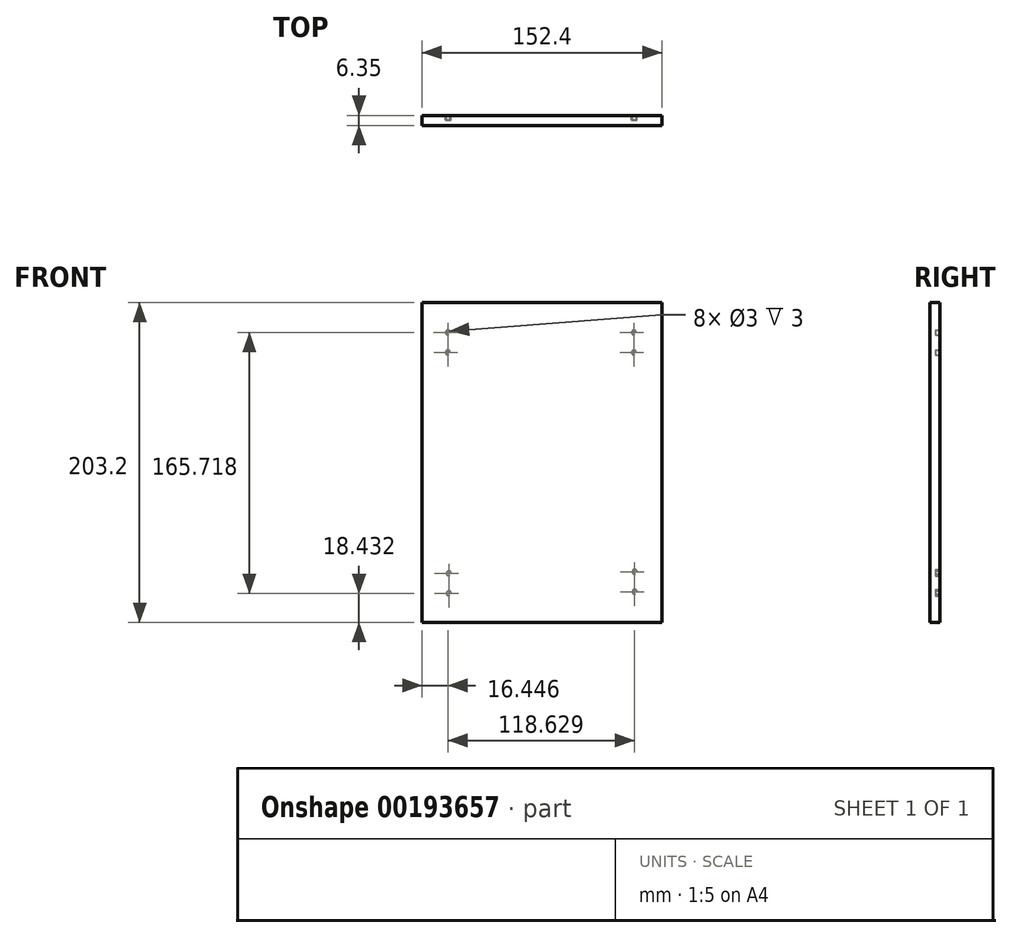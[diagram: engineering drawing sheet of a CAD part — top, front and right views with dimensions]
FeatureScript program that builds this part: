
annotation { "Feature Type Name" : "Feature", "Feature Type Description" : "" }
export const myFeature = defineFeature(function(context is Context, id is Id, definition is map)
    precondition{}
    {
        {
            var Q0;
            Q0=qCreatedBy(makeId("Front.planeOp"),FACE);
            var sketch = newSketch(context, id + "F0", { "sketchPlane" : qUnion([Q0])});
            skLineSegment(sketch, "E0.bottom", {"start": v(76.2, -101.6) * mm, "end": v(-76.2, -101.6) * mm});
            skLineSegment(sketch, "E0.top", {"start": v(76.2, 101.6) * mm, "end": v(-76.2, 101.6) * mm});
            skLineSegment(sketch, "E0.left", {"start": v(76.2, -101.6) * mm, "end": v(76.2, 101.6) * mm});
            skLineSegment(sketch, "E0.right", {"start": v(-76.2, -101.6) * mm, "end": v(-76.2, 101.6) * mm});
            skPoint(sketch, "E0.middle", {"position": v(0, 0) * mm});
            skSolve(sketch);
        }
        {
            var Q0;
            Q0=makeQuery(id+"F0.imprint","IMPRINT",FACE,{"disambiguationData":[TD([[makeQuery(id+"F0.imprint","IMPRINT",EDGE,{"derivedFrom":sQuery(id+"F0.wireOp",EDGE,"E0.bottom")}),-1.0]])]});
            extrude(context, id + "F1", {"entities" : qUnion([Q0]), "depth" : 6.35 * mm});
        }
        {
            var Q0;
            Q0=makeQuery(id+"F1.opExtrude","CAP_FACE",FACE,{"disambiguationData":[OSD([sQuery(id+"F0.wireOp",EDGE,"E0.bottom"),sQuery(id+"F0.wireOp",EDGE,"E0.top"),sQuery(id+"F0.wireOp",EDGE,"E0.left"),sQuery(id+"F0.wireOp",EDGE,"E0.right")])],"isStart":true});
            var sketch = newSketch(context, id + "F2", { "sketchPlane" : qUnion([Q0])});
            skLineSegment(sketch, "E1", {"start": v(-58.44, 101.6) * mm, "end": v(-58.44, 82.55) * mm});
            skLineSegment(sketch, "E2", {"start": v(-58.44, 82.55) * mm, "end": v(-58.44, 69.85) * mm});
            skCircle(sketch, "E3", {"center": v(-58.44, 69.85) * mm, "radius": 1.5 * mm});
            skCircle(sketch, "E4", {"center": v(-58.44, 82.55) * mm, "radius": 1.5 * mm});
            skSolve(sketch);
        }
        {
            var Q0;
            Q0=makeQuery(id+"F2.imprint","IMPRINT",FACE,{"disambiguationData":[TD([[makeQuery(id+"F2.imprint","IMPRINT",EDGE,{"derivedFrom":makeQuery(id+"F1.opExtrude","CAP_EDGE",EDGE,{"disambiguationData":[OSD([sQuery(id+"F0.wireOp",EDGE,"E0.bottom")])],"isStart":true})}),1.0]])]});
            var sketch = newSketch(context, id + "F3", { "sketchPlane" : qUnion([Q0])});
            skLineSegment(sketch, "E5", {"start": v(59.13, -102.22) * mm, "end": v(59.13, -83.17) * mm});
            skLineSegment(sketch, "E6", {"start": v(59.13, -83.17) * mm, "end": v(59.13, -70.47) * mm});
            skCircle(sketch, "E7", {"center": v(59.13, -83.17) * mm, "radius": 1.5 * mm});
            skCircle(sketch, "E8", {"center": v(59.13, -70.47) * mm, "radius": 1.5 * mm});
            skSolve(sketch);
        }
        {
            var Q0;
            Q0=makeQuery(id+"F2.imprint","IMPRINT",FACE,{"disambiguationData":[TD([[makeQuery(id+"F2.imprint","IMPRINT",EDGE,{"derivedFrom":makeQuery(id+"F1.opExtrude","CAP_EDGE",EDGE,{"disambiguationData":[OSD([sQuery(id+"F0.wireOp",EDGE,"E0.bottom")])],"isStart":true})}),1.0]])]});
            var sketch = newSketch(context, id + "F4", { "sketchPlane" : qUnion([Q0])});
            skLineSegment(sketch, "E9", {"start": v(-58.87, -101.22) * mm, "end": v(-58.87, -82.17) * mm});
            skLineSegment(sketch, "E10", {"start": v(-58.87, -82.17) * mm, "end": v(-58.87, -69.47) * mm});
            skCircle(sketch, "E11", {"center": v(-58.87, -82.17) * mm, "radius": 1.5 * mm});
            skCircle(sketch, "E12", {"center": v(-58.87, -69.47) * mm, "radius": 1.5 * mm});
            skSolve(sketch);
        }
        {
            var Q0;
            Q0 = qSketchRegion(id + "F4", true);
            extrude(context, id + "F5", {"entities" : qUnion([Q0]), "operationType" : NewBodyOperationType.REMOVE, "oppositeDirection" : true, "depth" : 3 * mm});
        }
        {
            var Q0;
            Q0 = qSketchRegion(id + "F3", true);
            extrude(context, id + "F6", {"entities" : qUnion([Q0]), "operationType" : NewBodyOperationType.REMOVE, "oppositeDirection" : true, "depth" : 3 * mm});
        }
        {
            var Q0;
            Q0 = qSketchRegion(id + "F2", true);
            extrude(context, id + "F7", {"entities" : qUnion([Q0]), "operationType" : NewBodyOperationType.REMOVE, "oppositeDirection" : true, "depth" : 3 * mm});
        }
        {
            var Q0;
            Q0=makeQuery(id+"F1.opExtrude","CAP_FACE",FACE,{"disambiguationData":[OSD([sQuery(id+"F0.wireOp",EDGE,"E0.bottom"),sQuery(id+"F0.wireOp",EDGE,"E0.top"),sQuery(id+"F0.wireOp",EDGE,"E0.left"),sQuery(id+"F0.wireOp",EDGE,"E0.right")])],"isStart":true});
            var sketch = newSketch(context, id + "F8", { "sketchPlane" : qUnion([Q0])});
            skLineSegment(sketch, "E13", {"start": v(59.64, 101.6) * mm, "end": v(59.75, 82.55) * mm});
            skLineSegment(sketch, "E14", {"start": v(59.75, 82.55) * mm, "end": v(59.7, 69.85) * mm});
            skPoint(sketch, "E14.endSnap0", {"position": v(59.7, 92.08) * mm});
            skCircle(sketch, "E15", {"center": v(59.75, 82.55) * mm, "radius": 1.5 * mm});
            skCircle(sketch, "E16", {"center": v(59.7, 69.85) * mm, "radius": 1.5 * mm});
            skSolve(sketch);
        }
        {
            var Q0;
            Q0 = qSketchRegion(id + "F8", true);
            extrude(context, id + "F9", {"entities" : qUnion([Q0]), "operationType" : NewBodyOperationType.REMOVE, "oppositeDirection" : true, "depth" : 3 * mm});
        }
    });
